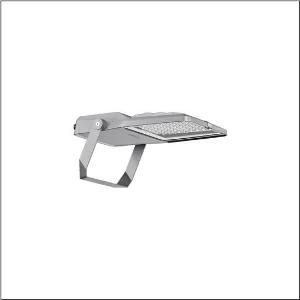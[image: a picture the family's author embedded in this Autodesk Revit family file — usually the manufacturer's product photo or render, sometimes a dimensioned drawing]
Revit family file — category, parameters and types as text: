
# Revit family: floodlight_fl_21_iq_mini___rs12_5xa7772d3b1a_ff90
name_source: partatom
category: Lighting Fixtures
units: mm (PartAtom-declared; Revit-internal decimal feet)

## family parameters
Cut with Voids When Loaded = No
Host = Face
Light Source = No
Part Type = Normal
Room Calculation Point = No
Round Connector Dimension = Use Diameter
Shared = No

## types (1)
- --- (1 x LED, 15500 lm, 143 W, 3000K)
    Apparent Load = 143 VA
    CIE Flux Codes = 79 92 99 100 100
    Color Rendering = 80
    Color Temperature = 3000K
    Default Elevation = 1800 mm
    Description = Floodlight FL 21 iQ mini, floodlight, primary light control with lens, of PMMA, primary optical cover: protective disc, of toughened safety glass, transparent, light distribution: RS12, light emission: direct distribution, installation type: surface-mounted, lamps: LED, High Power LED, rated values: 15.500lm | 143W | 108,4lm/W (begin service life); end service life: 15.500lm | 151,6W; at 50% lumin. flux: 7.750lm | 60,5W | 128,1lm/W, colour temperature: 3000K, colour rendering: CRI > 80, light colour: 830, light setting 1 begin service life: 100% | 15.500lm | 143W | 108,4lm/W | 3.000K, light setting 1 end service life: 151,6W, further light settings possible, control: Street-Remote, Auto-Match, Temp-Guard, Night-Set, Smart-Wire, Desk-Remote (wireless, voltage-free reading and setting of iQ features in the workshop via application-optimized NFC function/RFID function), optimised constant luminous flux control (CLO 2.0), pre-setting: linear dimming characteristic, with terminal, 6-pole, mains connection: 220..240V, AC, 50/60Hz, luminaire housing, of diecast aluminium, powder-coated, SITECO metallic grey (DB 702S), corrosivity category C5 mid according to DIN EN ISO 12944suitable for swimming poolschlorine-resistant, sealing non-destructively replaceable, mounting bracket, of steel, galvanised, powder-coated, SITECO metallic grey (DB 702S), protection rating (complete): IP66, insulation class (complete): insulation class II (safety insulation), certification: CE, ENEC, VDE, protection symbol: D, impact resistance: IK08, permissible operating ambient temperature: -40..+40°C, permissible operating ambient temperature for outdoor applications: -40..+50°C, standard: DIN EN 12944, LABS conformity tested according to VDMA 24364:2018-05, packaging unit: 1 piece

Light Distribution: RS12
    Height = 70 mm
    Lamp = 1 x LED
    Lamp Light Flux = 15500 lm
    Lamp Power = 143 W
    Lamp count = 1
    Length = 485 mm
    Luminous efficacy = 108 lm/W
    Manufacturer = Siteco
    ModVariant = No
    Model = 5XA7772D3B1A
    Mounting Place = Pole
    Mounting Type = Pole annexe
    Number of Poles = 1
    OnlyDefault = Yes
    Power Factor = 1
    Product Name = Floodlight FL 21 iQ mini | RS12
    Product group = floodlight | pylon annexe
    ProductGroupID = 6201
    Protection Class = Protection class II
    Protection Degree = IP 66
    RLX_Detail_Level = 1
    RLX_Emergency_Light_Flux = 0 lm
    RLX_Emergency_Type = 0
    RLX_Emergency_Type_DB = No
    RlxData = <blob elided: 91385 chars, md5=c38b6170>
    Socket = socket
    Standby Power = 0 W
    System Light Flux = 15500 lm
    System Power = 143 W
    Type Comments = factory setting: luminous flux: 100 % | dim-lin: 254 | 730 mA
    Type Image = l_1006845.jpg
    URL = http://relux.com
    VarID = @adj_168371
    Voltage = 0 V
    Weight = 0.00 kg
    Width = 337 mm

## geometry (parser evidence)
native form markers: Blend x4, Sweep x14
no freeform markers — native parametric forms only
